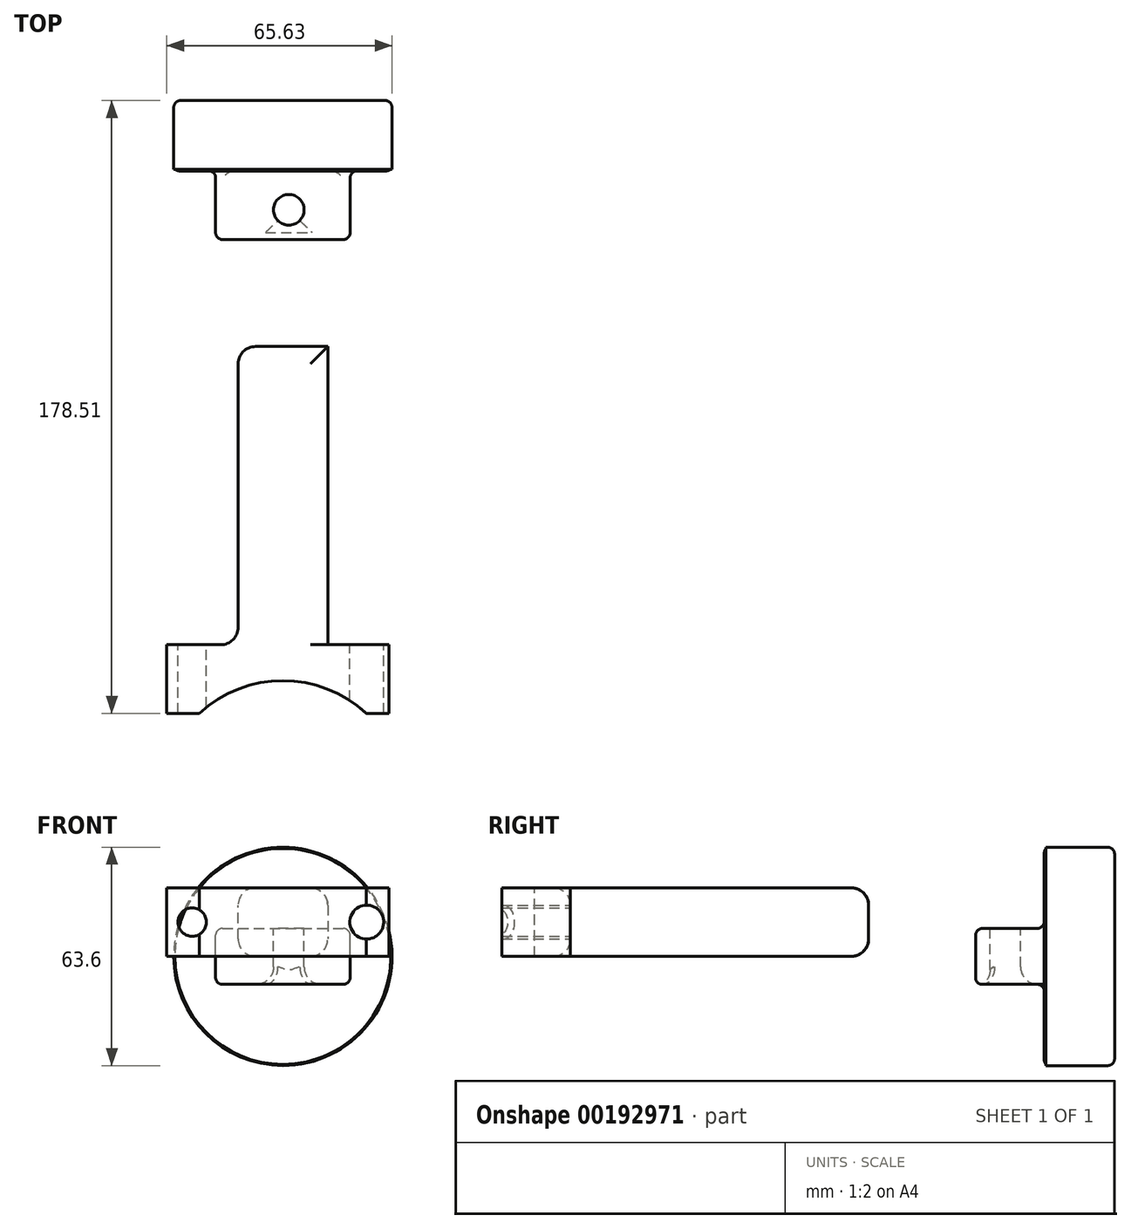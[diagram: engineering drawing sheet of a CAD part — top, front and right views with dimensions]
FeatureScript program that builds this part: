
annotation { "Feature Type Name" : "Feature", "Feature Type Description" : "" }
export const myFeature = defineFeature(function(context is Context, id is Id, definition is map)
    precondition{}
    {
        {
            var Q0;
            Q0=qCreatedBy(makeId("Front.planeOp"),FACE);
            var sketch = newSketch(context, id + "F0", { "sketchPlane" : qUnion([Q0])});
            skCircle(sketch, "E0", {"center": v(0, 0) * mm, "radius": 31.8 * mm});
            skSolve(sketch);
        }
        {
            var Q0;
            Q0 = qSketchRegion(id + "F0", true);
            extrude(context, id + "F1", {"entities" : qUnion([Q0]), "depth" : 20 * mm});
        }
        {
            var Q0;
            Q0=makeQuery(id+"F1.opExtrude","CAP_FACE",FACE,{"disambiguationData":[OSD([sQuery(id+"F0.wireOp",EDGE,"E0"),sQuery(id+"F0.wireOp",EDGE,"JONBwOeJ-JAso-ALg4-Y8q6-jQH0n12qDV8q")])],"isStart":false});
            var sketch = newSketch(context, id + "F2", { "sketchPlane" : qUnion([Q0])});
            skCircle(sketch, "E1", {"center": v(0, 0) * mm, "radius": 31.44 * mm});
            skSolve(sketch);
        }
        {
            var Q0;
            Q0 = qSketchRegion(id + "F2", true);
            extrude(context, id + "F3", {"entities" : qUnion([Q0]), "operationType" : NewBodyOperationType.ADD, "depth" : 0.5 * mm});
        }
        {
            var Q0;
            Q0=makeQuery(id+"F3.opExtrude","CAP_FACE",FACE,{"disambiguationData":[OSD([sQuery(id+"F2.wireOp",EDGE,"E1")])],"isStart":false});
            var Q1;
            Q1=makeQuery(id+"F1.opExtrude","CAP_EDGE",EDGE,{"disambiguationData":[OSD([sQuery(id+"F0.wireOp",EDGE,"E0")])],"isStart":true});
            fillet(context, id + "F4", {"entities" : qUnion([Q0, Q1]), "radius" : 2 * mm, "tangentPropagation" : true, "allowEdgeOverflow" : false});
        }
        {
            var Q0;
            Q0=makeQuery(id+"F3.opExtrude","CAP_FACE",FACE,{"disambiguationData":[OSD([sQuery(id+"F2.wireOp",EDGE,"E1")])],"isStart":false});
            var sketch = newSketch(context, id + "F5", { "sketchPlane" : qUnion([Q0])});
            skLineSegment(sketch, "E2.bottom", {"start": v(-19.6, -8.16) * mm, "end": v(19.6, -8.16) * mm});
            skLineSegment(sketch, "E2.top", {"start": v(-19.6, 8.16) * mm, "end": v(19.6, 8.16) * mm});
            skLineSegment(sketch, "E2.left", {"start": v(-19.6, -8.16) * mm, "end": v(-19.6, 8.16) * mm});
            skLineSegment(sketch, "E2.right", {"start": v(19.6, -8.16) * mm, "end": v(19.6, 8.16) * mm});
            skPoint(sketch, "E2.middle", {"position": v(0, 0) * mm});
            skSolve(sketch);
        }
        {
            var Q0;
            Q0 = qSketchRegion(id + "F5", true);
            extrude(context, id + "F6", {"entities" : qUnion([Q0]), "operationType" : NewBodyOperationType.ADD, "depth" : 20 * mm});
        }
        {
            var Q0;
            Q0=makeQuery(id+"F6.opExtrude","SWEPT_FACE",FACE,{"disambiguationData":[OSD([sQuery(id+"F5.wireOp",EDGE,"E2.top")])]});
            var Q1;
            Q1=makeQuery(id+"F6.opExtrude","CAP_EDGE",EDGE,{"disambiguationData":[OSD([sQuery(id+"F5.wireOp",EDGE,"E2.bottom")])],"isStart":false});
            var Q2;
            Q2=makeQuery(id+"F6.opExtrude","SWEPT_FACE",FACE,{"disambiguationData":[OSD([sQuery(id+"F5.wireOp",EDGE,"E2.left")])]});
            var Q3;
            Q3=makeQuery(id+"F6.opExtrude","SWEPT_FACE",FACE,{"disambiguationData":[OSD([sQuery(id+"F5.wireOp",EDGE,"E2.right")])]});
            fillet(context, id + "F7", {"entities" : qUnion([Q0, Q1, Q2, Q3]), "radius" : 2 * mm, "tangentPropagation" : true, "allowEdgeOverflow" : false});
        }
        {
            var Q0;
            Q0=makeQuery(id+"F6.opExtrude","SWEPT_FACE",FACE,{"disambiguationData":[OSD([sQuery(id+"F5.wireOp",EDGE,"E2.top")])]});
            var sketch = newSketch(context, id + "F8", { "sketchPlane" : qUnion([Q0])});
            skCircle(sketch, "E3", {"center": v(1.73, -31.84) * mm, "radius": 4.46 * mm});
            skSolve(sketch);
        }
        {
            var Q0;
            Q0 = qSketchRegion(id + "F8", true);
            extrude(context, id + "F9", {"entities" : qUnion([Q0]), "operationType" : NewBodyOperationType.REMOVE, "oppositeDirection" : true, "depth" : 25.4 * mm});
        }
        {
            var Q0;
            Q0=makeQuery(id+"F9.boolean.opBoolean","INTERSECT",EDGE,{"derivedFrom":[makeQuery(id+"F6.opExtrude","SWEPT_FACE",FACE,{"disambiguationData":[OSD([sQuery(id+"F5.wireOp",EDGE,"E2.bottom")])]}),makeQuery(id+"F9.opExtrude","SWEPT_FACE",FACE,{"disambiguationData":[OSD([sQuery(id+"F8.wireOp",EDGE,"E3")])]})]});
            var Q1;
            Q1=makeQuery(id+"F9.boolean.opBoolean","COPY",EDGE,{"derivedFrom":makeQuery(id+"F9.opExtrude","CAP_EDGE",EDGE,{"disambiguationData":[OSD([sQuery(id+"F8.wireOp",EDGE,"E3")])],"isStart":true})});
            fillet(context, id + "F10", {"entities" : qUnion([Q0, Q1]), "radius" : 5.08 * mm, "tangentPropagation" : true, "allowEdgeOverflow" : false});
        }
        {
            var Q0;
            Q0=qCreatedBy(makeId("Top.planeOp"),FACE);
            var sketch = newSketch(context, id + "F11", { "sketchPlane" : qUnion([Q0])});
            skLineSegment(sketch, "E4.bottom", {"start": v(-13.07, -49.84) * mm, "end": v(13.07, -49.84) * mm});
            skLineSegment(sketch, "E4.top", {"start": v(-13.07, -158.52) * mm, "end": v(13.07, -158.52) * mm});
            skLineSegment(sketch, "E4.left", {"start": v(-13.07, -49.84) * mm, "end": v(-13.07, -158.52) * mm});
            skLineSegment(sketch, "E4.right", {"start": v(13.07, -49.84) * mm, "end": v(13.07, -158.52) * mm});
            skPoint(sketch, "E4.middle", {"position": v(0, -104.18) * mm});
            skSolve(sketch);
        }
        {
            var Q0;
            Q0=makeQuery(id+"F11.imprint","IMPRINT",FACE,{"disambiguationData":[TD([[makeQuery(id+"F11.imprint","IMPRINT",EDGE,{"derivedFrom":sQuery(id+"F11.wireOp",EDGE,"E4.bottom")}),-1.0]])]});
            extrude(context, id + "F12", {"entities" : qUnion([Q0]), "depth" : 20 * mm});
        }
        {
            var Q0;
            Q0=makeQuery(id+"F12.opExtrude","SWEPT_FACE",FACE,{"disambiguationData":[OSD([sQuery(id+"F11.wireOp",EDGE,"E4.right")])]});
            var sketch = newSketch(context, id + "F13", { "sketchPlane" : qUnion([Q0])});
            skLineSegment(sketch, "E5.bottom", {"start": v(-71.67, 4.44) * mm, "end": v(-49.84, 4.44) * mm});
            skLineSegment(sketch, "E5.top", {"start": v(-71.67, 16.42) * mm, "end": v(-49.84, 16.42) * mm});
            skLineSegment(sketch, "E5.left", {"start": v(-71.67, 4.44) * mm, "end": v(-71.67, 16.42) * mm});
            skLineSegment(sketch, "E5.right", {"start": v(-49.84, 4.44) * mm, "end": v(-49.84, 16.42) * mm});
            skSolve(sketch);
        }
        {
            var Q0;
            Q0 = qSketchRegion(id + "F13", true);
            extrude(context, id + "F14", {"entities" : qUnion([Q0]), "operationType" : NewBodyOperationType.REMOVE, "oppositeDirection" : true, "depth" : 38.1 * mm});
        }
        {
            var Q0;
            Q0=makeQuery(id+"F12.opExtrude","CAP_EDGE",EDGE,{"disambiguationData":[OSD([sQuery(id+"F11.wireOp",EDGE,"E4.bottom")])],"isStart":false});
            var Q1;
            Q1=makeQuery(id+"F12.opExtrude","CAP_EDGE",EDGE,{"disambiguationData":[OSD([sQuery(id+"F11.wireOp",EDGE,"E4.bottom")])],"isStart":true});
            fillet(context, id + "F15", {"entities" : qUnion([Q0, Q1]), "radius" : 5.08 * mm, "tangentPropagation" : true, "allowEdgeOverflow" : false});
        }
        {
            var Q0;
            Q0=makeQuery(id+"F14.boolean.opBoolean","INTERSECT",EDGE,{"derivedFrom":[makeQuery(id+"F12.opExtrude","SWEPT_FACE",FACE,{"disambiguationData":[OSD([sQuery(id+"F11.wireOp",EDGE,"E4.left")])]}),makeQuery(id+"F14.opExtrude","SWEPT_FACE",FACE,{"disambiguationData":[OSD([sQuery(id+"F13.wireOp",EDGE,"E5.bottom")])]})]});
            var Q1;
            Q1=makeQuery(id+"F14.boolean.opBoolean","INTERSECT",EDGE,{"derivedFrom":[makeQuery(id+"F12.opExtrude","SWEPT_FACE",FACE,{"disambiguationData":[OSD([sQuery(id+"F11.wireOp",EDGE,"E4.left")])]}),makeQuery(id+"F14.opExtrude","SWEPT_FACE",FACE,{"disambiguationData":[OSD([sQuery(id+"F13.wireOp",EDGE,"E5.top")])]})]});
            var Q2;
            Q2=makeQuery(id+"F14.boolean.opBoolean","COPY",EDGE,{"derivedFrom":makeQuery(id+"F14.opExtrude","CAP_EDGE",EDGE,{"disambiguationData":[OSD([sQuery(id+"F13.wireOp",EDGE,"E5.bottom")])],"isStart":true})});
            var Q3;
            Q3=makeQuery(id+"F14.boolean.opBoolean","COPY",EDGE,{"derivedFrom":makeQuery(id+"F14.opExtrude","CAP_EDGE",EDGE,{"disambiguationData":[OSD([sQuery(id+"F13.wireOp",EDGE,"E5.top")])],"isStart":true})});
            fillet(context, id + "F16", {"entities" : qUnion([Q0, Q1, Q2, Q3]), "radius" : 5.08 * mm, "tangentPropagation" : true, "allowEdgeOverflow" : false});
        }
        {
            var Q0;
            Q0=makeQuery(id+"F14.boolean.opBoolean","INTERSECT",EDGE,{"derivedFrom":[makeQuery(id+"F12.opExtrude","SWEPT_FACE",FACE,{"disambiguationData":[OSD([sQuery(id+"F11.wireOp",EDGE,"E4.left")])]}),makeQuery(id+"F14.opExtrude","SWEPT_FACE",FACE,{"disambiguationData":[OSD([sQuery(id+"F13.wireOp",EDGE,"E5.left")])]})]});
            var Q1;
            Q1=makeQuery(id+"F14.boolean.opBoolean","COPY",EDGE,{"derivedFrom":makeQuery(id+"F14.opExtrude","CAP_EDGE",EDGE,{"disambiguationData":[OSD([sQuery(id+"F13.wireOp",EDGE,"E5.left")])],"isStart":true})});
            fillet(context, id + "F17", {"entities" : qUnion([Q0, Q1]), "radius" : 5.08 * mm, "tangentPropagation" : true, "allowEdgeOverflow" : false});
        }
        {
            var Q0;
            Q0=makeQuery(id+"F12.opExtrude","CAP_FACE",FACE,{"disambiguationData":[OSD([sQuery(id+"F11.wireOp",EDGE,"E4.bottom"),sQuery(id+"F11.wireOp",EDGE,"E4.top"),sQuery(id+"F11.wireOp",EDGE,"E4.left"),sQuery(id+"F11.wireOp",EDGE,"E4.right")])],"isStart":false});
            var sketch = newSketch(context, id + "F18", { "sketchPlane" : qUnion([Q0])});
            skCircle(sketch, "E6", {"center": v(0, -64.45) * mm, "radius": 5.85 * mm});
            skSolve(sketch);
        }
        {
            var Q0;
            Q0 = qSketchRegion(id + "F18", true);
            extrude(context, id + "F19", {"entities" : qUnion([Q0]), "operationType" : NewBodyOperationType.REMOVE, "oppositeDirection" : true, "depth" : 25.4 * mm});
        }
        {
            var Q0;
            Q0=makeQuery(id+"F12.opExtrude","CAP_FACE",FACE,{"disambiguationData":[OSD([sQuery(id+"F11.wireOp",EDGE,"E4.bottom"),sQuery(id+"F11.wireOp",EDGE,"E4.top"),sQuery(id+"F11.wireOp",EDGE,"E4.left"),sQuery(id+"F11.wireOp",EDGE,"E4.right")])],"isStart":false});
            var sketch = newSketch(context, id + "F20", { "sketchPlane" : qUnion([Q0])});
            skLineSegment(sketch, "E7.bottom", {"start": v(-25.89, -178.51) * mm, "end": v(-24.32, -178.51) * mm});
            skLineSegment(sketch, "E7.top", {"start": v(-25.89, -158.52) * mm, "end": v(22.99, -158.52) * mm});
            skLineSegment(sketch, "E7.left", {"start": v(-33.83, -170.57) * mm, "end": v(-33.83, -166.46) * mm});
            skLineSegment(sketch, "E7.right", {"start": v(30.93, -170.57) * mm, "end": v(30.93, -166.46) * mm});
            skPoint(sketch, "E8.visualSharp", {"position": v(-33.83, -178.51) * mm});
            skPoint(sketch, "E9.visualSharp", {"position": v(30.93, -178.51) * mm});
            skPoint(sketch, "E10.visualSharp", {"position": v(30.93, -158.52) * mm});
            skPoint(sketch, "E11.visualSharp", {"position": v(-33.83, -158.52) * mm});
            skLineSegment(sketch, "E12", {"start": v(-25.89, -178.51) * mm, "end": v(-33.83, -178.51) * mm});
            skLineSegment(sketch, "E13", {"start": v(-33.83, -178.51) * mm, "end": v(-33.83, -158.52) * mm});
            skLineSegment(sketch, "E14", {"start": v(-33.83, -158.52) * mm, "end": v(-25.89, -158.52) * mm});
            skLineSegment(sketch, "E15", {"start": v(22.99, -178.51) * mm, "end": v(30.93, -178.51) * mm});
            skLineSegment(sketch, "E16", {"start": v(30.93, -178.51) * mm, "end": v(30.93, -158.52) * mm});
            skLineSegment(sketch, "E17", {"start": v(30.93, -158.52) * mm, "end": v(22.99, -158.52) * mm});
            skArc(sketch, "E18", {"start": v(24.32, -178.51) * mm, "mid": v(0, -169) * mm, "end": v(-24.32, -178.51) * mm});
            skSolve(sketch);
        }
        {
            var Q0;
            Q0=makeQuery(id+"F20.imprint","IMPRINT",FACE,{"disambiguationData":[TD([[makeQuery(id+"F20.imprint","IMPRINT",EDGE,{"derivedFrom":sQuery(id+"F20.wireOp",EDGE,"E7.bottom")}),1.0]])]});
            extrude(context, id + "F21", {"entities" : qUnion([Q0]), "oppositeDirection" : true, "depth" : 20 * mm});
        }
        {
            var Q0;
            Q0=makeQuery(id+"F21.opExtrude","SWEPT_BODY",BODY,{"disambiguationData":[OSD([sQuery(id+"F20.wireOp",EDGE,"E7.bottom"),sQuery(id+"F20.wireOp",EDGE,"E7.top"),sQuery(id+"F20.wireOp",EDGE,"E7.left"),sQuery(id+"F20.wireOp",EDGE,"E7.right"),sQuery(id+"F20.wireOp",EDGE,"E8.filletArc"),sQuery(id+"F20.wireOp",EDGE,"E9.filletArc"),sQuery(id+"F20.wireOp",EDGE,"E10.filletArc"),sQuery(id+"F20.wireOp",EDGE,"E11.filletArc")])]});
            var Q1;
            Q1=makeQuery(id+"F12.opExtrude","SWEPT_BODY",BODY,{"disambiguationData":[OSD([sQuery(id+"F11.wireOp",EDGE,"E4.bottom"),sQuery(id+"F11.wireOp",EDGE,"E4.top"),sQuery(id+"F11.wireOp",EDGE,"E4.left"),sQuery(id+"F11.wireOp",EDGE,"E4.right")])]});
            booleanBodies(context, id + "F22", {"operationType" : BooleanOperationType.UNION, "tools" : qUnion([Q0, Q1])});
        }
        {
            var Q0;
            Q0=makeQuery(id+"F12.opExtrude","SWEPT_EDGE",EDGE,{"disambiguationData":[OSD([sQuery(id+"F11.wireOp",EDGE,"E4.top"),sQuery(id+"F11.wireOp",EDGE,"E4.left")])]});
            var Q1;
            Q1=makeQuery(id+"F21.opExtrude","SWEPT_EDGE",EDGE,{"disambiguationData":[OSD([sQuery(id+"F20.wireOp",EDGE,"E7.top"),sQuery(id+"F20.wireOp",EDGE,"E10.filletArc")])]});
            var Q2;
            Q2=makeQuery(id+"F12.opExtrude","SWEPT_EDGE",EDGE,{"disambiguationData":[OSD([sQuery(id+"F11.wireOp",EDGE,"E4.top"),sQuery(id+"F11.wireOp",EDGE,"E4.right")])]});
            fillet(context, id + "F23", {"entities" : qUnion([Q0, Q1, Q2]), "radius" : 5.08 * mm, "tangentPropagation" : true, "allowEdgeOverflow" : false});
        }
        {
            var Q0;
            Q0=makeQuery(id+"F12.opExtrude","CAP_EDGE",EDGE,{"disambiguationData":[OSD([sQuery(id+"F11.wireOp",EDGE,"E4.left")])],"isStart":false});
            var Q1;
            Q1=makeQuery(id+"F12.opExtrude","CAP_EDGE",EDGE,{"disambiguationData":[OSD([sQuery(id+"F11.wireOp",EDGE,"E4.left")])],"isStart":true});
            var Q2;
            Q2=makeQuery(id+"F12.opExtrude","CAP_EDGE",EDGE,{"disambiguationData":[OSD([sQuery(id+"F11.wireOp",EDGE,"E4.right")])],"isStart":true});
            var Q3;
            Q3=makeQuery(id+"F12.opExtrude","CAP_EDGE",EDGE,{"disambiguationData":[OSD([sQuery(id+"F11.wireOp",EDGE,"E4.right")])],"isStart":false});
            fillet(context, id + "F24", {"entities" : qUnion([Q0, Q1, Q2, Q3]), "radius" : 5.08 * mm, "tangentPropagation" : true, "allowEdgeOverflow" : false});
        }
        {
            var Q0;
            {var subQ1=sQuery(id+"F20.wireOp",EDGE,"E17");var subQ4=sQuery(id+"F20.wireOp",EDGE,"E14");var subQ7=sQuery(id+"F20.wireOp",EDGE,"E7.top");var subQ9=sQuery(id+"F11.wireOp",EDGE,"E4.right");Q0=makeQuery(id+"F22.opBoolean","SPLIT",FACE,{"disambiguationData":[TD([makeQuery(id+"F12.opExtrude","SWEPT_FACE",FACE,{"disambiguationData":[OSD([subQ9])]})])],"derivedFrom":makeQuery(id+"F21.opExtrude","SWEPT_FACE",FACE,{"disambiguationData":[OSD([subQ7,subQ4,subQ1])]})});}
            var sketch = newSketch(context, id + "F25", { "sketchPlane" : qUnion([Q0])});
            skCircle(sketch, "E19", {"center": v(-24.44, 10) * mm, "radius": 4.92 * mm});
            skPoint(sketch, "E19.centerSnap0", {"position": v(-30.93, 10) * mm});
            skCircle(sketch, "E20", {"center": v(26.42, 10) * mm, "radius": 4.13 * mm});
            skSolve(sketch);
        }
        {
            var Q0;
            Q0 = qSketchRegion(id + "F25", true);
            extrude(context, id + "F26", {"entities" : qUnion([Q0]), "operationType" : NewBodyOperationType.REMOVE, "oppositeDirection" : true, "depth" : 25.4 * mm});
        }
    });
